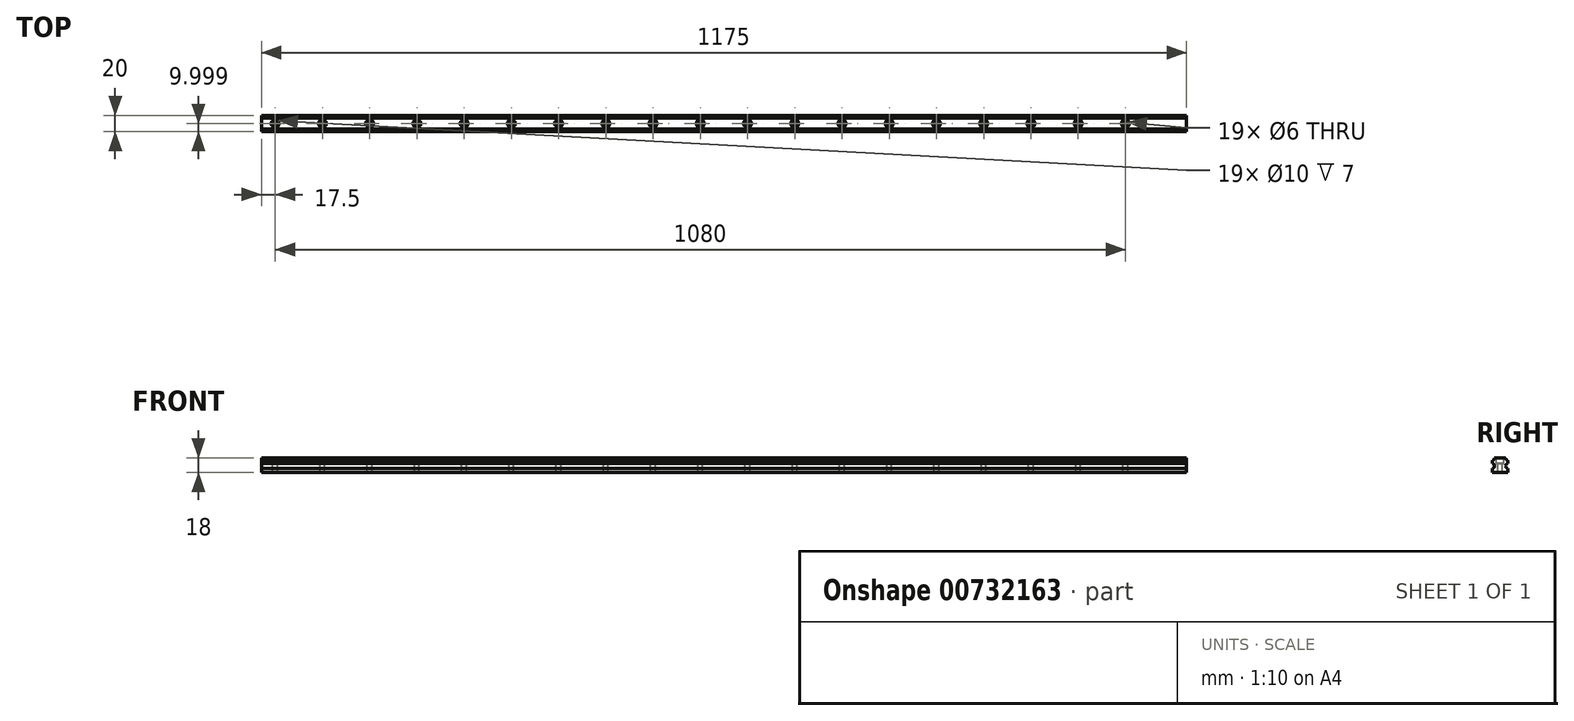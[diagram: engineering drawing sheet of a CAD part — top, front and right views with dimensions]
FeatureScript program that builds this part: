
annotation { "Feature Type Name" : "Feature", "Feature Type Description" : "" }
export const myFeature = defineFeature(function(context is Context, id is Id, definition is map)
    precondition{}
    {
        {
            var Q0;
            Q0=qCreatedBy(makeId("Right.planeOp"),FACE);
            var sketch = newSketch(context, id + "F0", { "sketchPlane" : qUnion([Q0])});
            skLineSegment(sketch, "E0", {"start": v(-26.04, 0) * mm, "end": v(-26.04, 5) * mm});
            skLineSegment(sketch, "E1", {"start": v(-26.04, 11) * mm, "end": v(-26.04, 15) * mm});
            skLineSegment(sketch, "E2", {"start": v(-23.04, 18) * mm, "end": v(-9.04, 18) * mm});
            skLineSegment(sketch, "E3", {"start": v(-6.04, 15) * mm, "end": v(-6.04, 11) * mm});
            skLineSegment(sketch, "E4", {"start": v(-6.04, 5) * mm, "end": v(-6.04, 0) * mm});
            skLineSegment(sketch, "E5", {"start": v(-6.04, 0) * mm, "end": v(-26.04, 0) * mm});
            skArc(sketch, "E6", {"start": v(-26.04, 5) * mm, "mid": v(-23.04, 8) * mm, "end": v(-26.04, 11) * mm});
            skArc(sketch, "E7", {"start": v(-6.04, 11) * mm, "mid": v(-9.04, 8) * mm, "end": v(-6.04, 5) * mm});
            skArc(sketch, "E8", {"start": v(-26.04, 15) * mm, "mid": v(-23.92, 15.88) * mm, "end": v(-23.04, 18) * mm});
            skArc(sketch, "E9", {"start": v(-9.04, 18) * mm, "mid": v(-8.16, 15.88) * mm, "end": v(-6.04, 15) * mm});
            skSolve(sketch);
        }
        {
            var Q0;
            Q0=qSketchRegion(id+"F0",true);
            extrude(context, id + "F1", {"entities" : qUnion([Q0]), "depth" : 1175 * mm, "offsetDistance" : 25 * mm});
        }
        {
            var Q0;
            Q0=makeQuery(id+"F1.opExtrude","SWEPT_FACE",FACE,{"disambiguationData":[OSD([sQuery(id+"F0.wireOp",EDGE,"E2")])]});
            var sketch = newSketch(context, id + "F2", { "sketchPlane" : qUnion([Q0])});
            skCircle(sketch, "E10", {"center": v(17.5, -16.04) * mm, "radius": 3 * mm});
            skCircle(sketch, "E11", {"center": v(77.5, -16.04) * mm, "radius": 3 * mm});
            skCircle(sketch, "E12", {"center": v(137.5, -16.04) * mm, "radius": 3 * mm});
            skCircle(sketch, "E13", {"center": v(197.5, -16.04) * mm, "radius": 3 * mm});
            skCircle(sketch, "E14", {"center": v(257.5, -16.04) * mm, "radius": 3 * mm});
            skCircle(sketch, "E15", {"center": v(317.5, -16.04) * mm, "radius": 3 * mm});
            skCircle(sketch, "E16", {"center": v(377.5, -16.04) * mm, "radius": 3 * mm});
            skCircle(sketch, "E17", {"center": v(437.5, -16.04) * mm, "radius": 3 * mm});
            skCircle(sketch, "E18", {"center": v(497.5, -16.04) * mm, "radius": 3 * mm});
            skCircle(sketch, "E19", {"center": v(557.5, -16.04) * mm, "radius": 3 * mm});
            skCircle(sketch, "E20", {"center": v(617.5, -16.04) * mm, "radius": 3 * mm});
            skCircle(sketch, "E21", {"center": v(677.5, -16.04) * mm, "radius": 3 * mm});
            skCircle(sketch, "E22", {"center": v(737.5, -16.04) * mm, "radius": 3 * mm});
            skCircle(sketch, "E23", {"center": v(797.5, -16.04) * mm, "radius": 3 * mm});
            skCircle(sketch, "E24", {"center": v(857.5, -16.04) * mm, "radius": 3 * mm});
            skCircle(sketch, "E25", {"center": v(917.5, -16.04) * mm, "radius": 3 * mm});
            skCircle(sketch, "E26", {"center": v(977.5, -16.04) * mm, "radius": 3 * mm});
            skCircle(sketch, "E27", {"center": v(1037.5, -16.04) * mm, "radius": 3 * mm});
            skCircle(sketch, "E28", {"center": v(1097.5, -16.04) * mm, "radius": 3 * mm});
            skSolve(sketch);
        }
        {
            var Q0;
            Q0=qSketchRegion(id+"F2",true);
            extrude(context, id + "F3", {"entities" : qUnion([Q0]), "operationType" : NewBodyOperationType.REMOVE, "oppositeDirection" : true, "depth" : 18 * mm});
        }
        {
            var Q0;
            Q0=makeQuery(id+"F1.opExtrude","SWEPT_FACE",FACE,{"disambiguationData":[OSD([sQuery(id+"F0.wireOp",EDGE,"E2")])]});
            var sketch = newSketch(context, id + "F4", { "sketchPlane" : qUnion([Q0])});
            skCircle(sketch, "E29", {"center": v(17.5, -16.04) * mm, "radius": 5 * mm});
            skCircle(sketch, "E30", {"center": v(77.5, -16.04) * mm, "radius": 5 * mm});
            skCircle(sketch, "E31", {"center": v(137.5, -16.04) * mm, "radius": 5 * mm});
            skCircle(sketch, "E32", {"center": v(197.5, -16.04) * mm, "radius": 5 * mm});
            skCircle(sketch, "E33", {"center": v(257.5, -16.04) * mm, "radius": 5 * mm});
            skCircle(sketch, "E34", {"center": v(317.5, -16.04) * mm, "radius": 5 * mm});
            skCircle(sketch, "E35", {"center": v(377.5, -16.04) * mm, "radius": 5 * mm});
            skCircle(sketch, "E36", {"center": v(437.5, -16.04) * mm, "radius": 5 * mm});
            skCircle(sketch, "E37", {"center": v(497.5, -16.04) * mm, "radius": 5 * mm});
            skCircle(sketch, "E38", {"center": v(557.5, -16.04) * mm, "radius": 5 * mm});
            skCircle(sketch, "E39", {"center": v(617.5, -16.04) * mm, "radius": 5 * mm});
            skCircle(sketch, "E40", {"center": v(677.5, -16.04) * mm, "radius": 5 * mm});
            skCircle(sketch, "E41", {"center": v(737.5, -16.04) * mm, "radius": 5 * mm});
            skCircle(sketch, "E42", {"center": v(797.5, -16.04) * mm, "radius": 5 * mm});
            skCircle(sketch, "E43", {"center": v(857.5, -16.04) * mm, "radius": 5 * mm});
            skCircle(sketch, "E44", {"center": v(917.5, -16.04) * mm, "radius": 5 * mm});
            skCircle(sketch, "E45", {"center": v(977.5, -16.04) * mm, "radius": 5 * mm});
            skCircle(sketch, "E46", {"center": v(1037.5, -16.04) * mm, "radius": 5 * mm});
            skCircle(sketch, "E47", {"center": v(1097.5, -16.04) * mm, "radius": 5 * mm});
            skSolve(sketch);
        }
        {
            var Q0;
            Q0=qSketchRegion(id+"F4",true);
            extrude(context, id + "F5", {"entities" : qUnion([Q0]), "operationType" : NewBodyOperationType.REMOVE, "oppositeDirection" : true, "depth" : 7 * mm});
        }
    });
